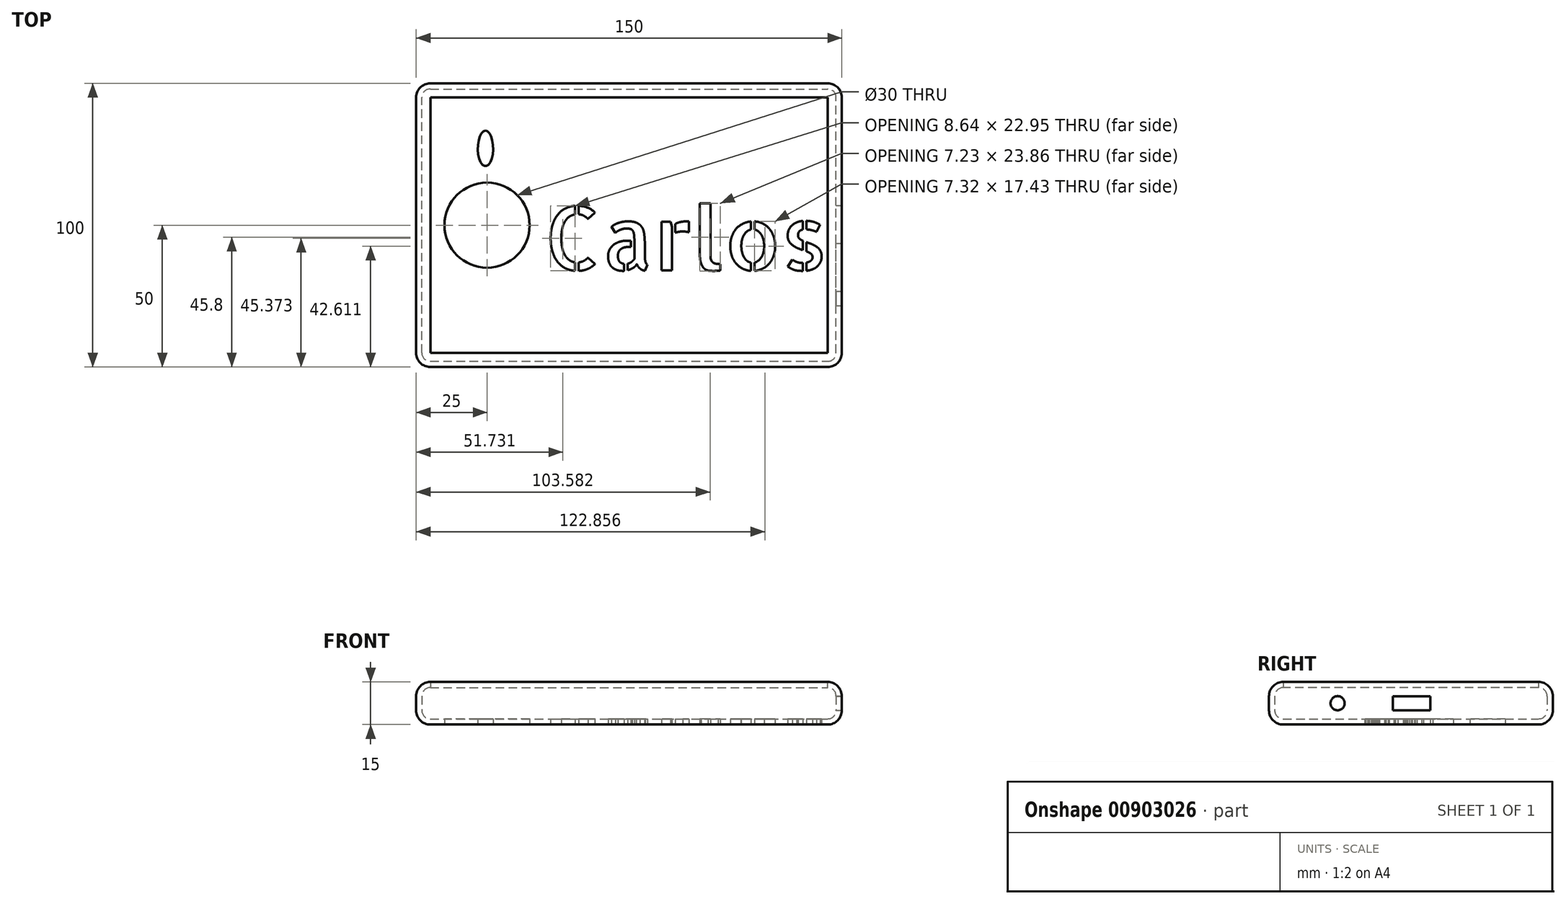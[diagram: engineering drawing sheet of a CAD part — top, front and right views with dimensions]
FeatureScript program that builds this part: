
annotation { "Feature Type Name" : "Feature", "Feature Type Description" : "" }
export const myFeature = defineFeature(function(context is Context, id is Id, definition is map)
    precondition{}
    {
        {
            var Q0;
            Q0=qCreatedBy(makeId("Top.planeOp"),FACE);
            var sketch = newSketch(context, id + "F0", { "sketchPlane" : qUnion([Q0])});
            skLineSegment(sketch, "E0.bottom", {"start": v(75, 50) * mm, "end": v(-75, 50) * mm});
            skLineSegment(sketch, "E0.top", {"start": v(75, -50) * mm, "end": v(-75, -50) * mm});
            skLineSegment(sketch, "E0.left", {"start": v(75, 50) * mm, "end": v(75, -50) * mm});
            skLineSegment(sketch, "E0.right", {"start": v(-75, 50) * mm, "end": v(-75, -50) * mm});
            skPoint(sketch, "E0.middle", {"position": v(0, 0) * mm});
            skSolve(sketch);
        }
        {
            var Q0;
            Q0 = qSketchRegion(id + "F0", true);
            extrude(context, id + "F1", {"entities" : qUnion([Q0]), "depth" : 15 * mm, "offsetDistance" : 25 * mm});
        }
        {
            var Q0;
            Q0=qCreatedBy(makeId("Top.planeOp"),FACE);
            var sketch = newSketch(context, id + "F2", { "sketchPlane" : qUnion([Q0])});
            skLineSegment(sketch, "E1.bottom", {"start": v(75, 50) * mm, "end": v(-75, 50) * mm});
            skLineSegment(sketch, "E1.top", {"start": v(75, -50) * mm, "end": v(-75, -50) * mm});
            skLineSegment(sketch, "E1.left", {"start": v(75, 50) * mm, "end": v(75, -50) * mm});
            skLineSegment(sketch, "E1.right", {"start": v(-75, 50) * mm, "end": v(-75, -50) * mm});
            skPoint(sketch, "E1.middle", {"position": v(0, 0) * mm});
            skSolve(sketch);
        }
        {
            var Q0;
            Q0=makeQuery(id+"F1.opExtrude","CAP_FACE",FACE,{"disambiguationData":[OSD([sQuery(id+"F0.wireOp",EDGE,"E0.bottom"),sQuery(id+"F0.wireOp",EDGE,"E0.top"),sQuery(id+"F0.wireOp",EDGE,"E0.left"),sQuery(id+"F0.wireOp",EDGE,"E0.right")])],"isStart":false});
            var Q1;
            Q1=makeQuery(id+"F1.opExtrude","SWEPT_EDGE",EDGE,{"disambiguationData":[OSD([sQuery(id+"F0.wireOp",EDGE,"E0.bottom"),sQuery(id+"F0.wireOp",EDGE,"E0.left")])]});
            var Q2;
            Q2=makeQuery(id+"F1.opExtrude","SWEPT_EDGE",EDGE,{"disambiguationData":[OSD([sQuery(id+"F0.wireOp",EDGE,"E0.top"),sQuery(id+"F0.wireOp",EDGE,"E0.left")])]});
            var Q3;
            Q3=makeQuery(id+"F1.opExtrude","SWEPT_EDGE",EDGE,{"disambiguationData":[OSD([sQuery(id+"F0.wireOp",EDGE,"E0.top"),sQuery(id+"F0.wireOp",EDGE,"E0.right")])]});
            var Q4;
            Q4=makeQuery(id+"F1.opExtrude","CAP_EDGE",EDGE,{"disambiguationData":[OSD([sQuery(id+"F0.wireOp",EDGE,"E0.bottom")])],"isStart":false});
            var Q5;
            Q5=makeQuery(id+"F1.opExtrude","CAP_EDGE",EDGE,{"disambiguationData":[OSD([sQuery(id+"F0.wireOp",EDGE,"E0.top")])],"isStart":true});
            var Q6;
            Q6=makeQuery(id+"F1.opExtrude","CAP_EDGE",EDGE,{"disambiguationData":[OSD([sQuery(id+"F0.wireOp",EDGE,"E0.top")])],"isStart":false});
            var Q7;
            Q7=makeQuery(id+"F1.opExtrude","CAP_EDGE",EDGE,{"disambiguationData":[OSD([sQuery(id+"F0.wireOp",EDGE,"E0.right")])],"isStart":false});
            var Q8;
            Q8=makeQuery(id+"F1.opExtrude","SWEPT_EDGE",EDGE,{"disambiguationData":[OSD([sQuery(id+"F0.wireOp",EDGE,"E0.bottom"),sQuery(id+"F0.wireOp",EDGE,"E0.right")])]});
            var Q9;
            Q9=makeQuery(id+"F1.opExtrude","CAP_EDGE",EDGE,{"disambiguationData":[OSD([sQuery(id+"F0.wireOp",EDGE,"E0.bottom")])],"isStart":true});
            var Q10;
            Q10=makeQuery(id+"F1.opExtrude","CAP_EDGE",EDGE,{"disambiguationData":[OSD([sQuery(id+"F0.wireOp",EDGE,"E0.left")])],"isStart":true});
            var Q11;
            Q11=makeQuery(id+"F1.opExtrude","CAP_EDGE",EDGE,{"disambiguationData":[OSD([sQuery(id+"F0.wireOp",EDGE,"E0.left")])],"isStart":false});
            var Q12;
            Q12=makeQuery(id+"F1.opExtrude","CAP_EDGE",EDGE,{"disambiguationData":[OSD([sQuery(id+"F0.wireOp",EDGE,"E0.right")])],"isStart":true});
            fillet(context, id + "F3", {"entities" : qUnion([Q0, Q1, Q2, Q3, Q4, Q5, Q6, Q7, Q8, Q9, Q10, Q11, Q12]), "radius" : 5 * mm, "tangentPropagation" : true, "allowEdgeOverflow" : false});
        }
        {
            var Q0;
            Q0=makeQuery(id+"F1.opExtrude","CAP_FACE",FACE,{"disambiguationData":[OSD([sQuery(id+"F0.wireOp",EDGE,"E0.bottom"),sQuery(id+"F0.wireOp",EDGE,"E0.top"),sQuery(id+"F0.wireOp",EDGE,"E0.left"),sQuery(id+"F0.wireOp",EDGE,"E0.right")])],"isStart":false});
            shell(context, id + "F4", {"entities" : qUnion([Q0]), "thickness" : 2 * mm});
        }
        {
            var Q0;
            Q0=makeQuery(id+"F2.imprint","IMPRINT",FACE,{"disambiguationData":[TD([[makeQuery(id+"F2.imprint","IMPRINT",EDGE,{"derivedFrom":sQuery(id+"F2.wireOp",EDGE,"E1.bottom")}),1.0]])]});
            var sketch = newSketch(context, id + "F5", { "sketchPlane" : qUnion([Q0])});
            skCircle(sketch, "E2", {"center": v(-50, 0) * mm, "radius": 15 * mm});
            skEllipse(sketch, "E3", {"center": v(-50.56, 27.05) * mm, "majorRadius": 6.23 * mm, "minorRadius": 2.7 * mm, "majorAxis": v(0, 1)});
            skSolve(sketch);
        }
        {
            var Q0;
            Q0 = qSketchRegion(id + "F5", true);
            extrude(context, id + "F6", {"entities" : qUnion([Q0]), "operationType" : NewBodyOperationType.REMOVE, "depth" : 25 * mm, "offsetDistance" : 25 * mm});
        }
        {
            var Q0;
            Q0=makeQuery(id+"F1.opExtrude","SWEPT_FACE",FACE,{"disambiguationData":[OSD([sQuery(id+"F0.wireOp",EDGE,"E0.left")])]});
            var sketch = newSketch(context, id + "F7", { "sketchPlane" : qUnion([Q0])});
            skLineSegment(sketch, "E4.bottom", {"start": v(-6.41, 10) * mm, "end": v(6.9, 10) * mm});
            skLineSegment(sketch, "E4.top", {"start": v(-6.41, 5) * mm, "end": v(6.9, 5) * mm});
            skLineSegment(sketch, "E4.left", {"start": v(-6.41, 10) * mm, "end": v(-6.41, 5) * mm});
            skLineSegment(sketch, "E4.right", {"start": v(6.9, 10) * mm, "end": v(6.9, 5) * mm});
            skCircle(sketch, "E5", {"center": v(-25.82, 7.52) * mm, "radius": 2.5 * mm});
            skSolve(sketch);
        }
        {
            var Q0;
            Q0 = qSketchRegion(id + "F7", true);
            extrude(context, id + "F8", {"entities" : qUnion([Q0]), "operationType" : NewBodyOperationType.REMOVE, "oppositeDirection" : true, "depth" : 25 * mm, "offsetDistance" : 25 * mm});
        }
        {
            var Q0;
            Q0=makeQuery(id+"F2.imprint","IMPRINT",FACE,{"disambiguationData":[TD([[makeQuery(id+"F2.imprint","IMPRINT",EDGE,{"derivedFrom":sQuery(id+"F2.wireOp",EDGE,"E1.bottom")}),1.0]])]});
            var sketch = newSketch(context, id + "F9", { "sketchPlane" : qUnion([Q0])});
            skText(sketch, "E6", { "text": "Carlos", "fontName": "AllertaStencil-Regular.ttf"});
            const initialGuessF9  = {"E6": [-0.03, -0.01598, 1, 0, 0.0225]};
            skSetInitialGuess(sketch, initialGuessF9);
            skSolve(sketch);
        }
        {
            var Q0;
            Q0 = qSketchRegion(id + "F9", true);
            extrude(context, id + "F10", {"entities" : qUnion([Q0]), "operationType" : NewBodyOperationType.REMOVE, "depth" : 26.7 * mm, "offsetDistance" : 25 * mm});
        }
    });
